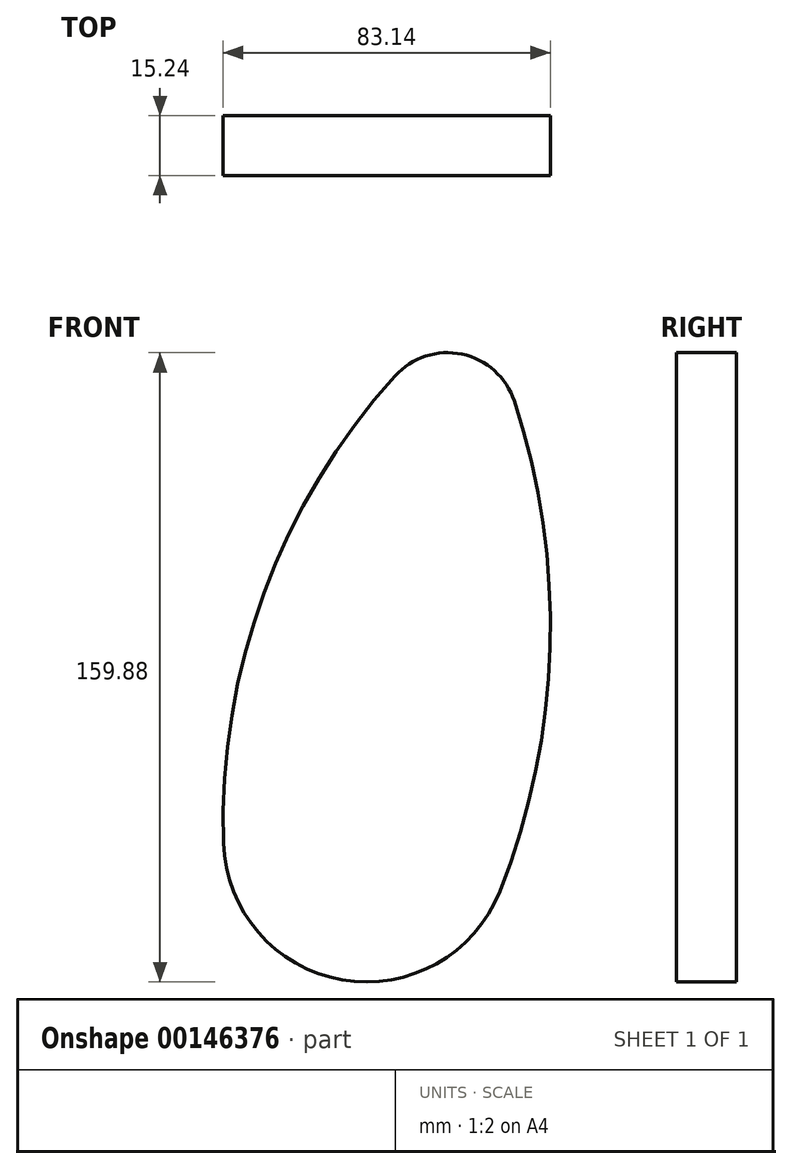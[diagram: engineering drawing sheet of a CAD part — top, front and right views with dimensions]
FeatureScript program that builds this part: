
annotation { "Feature Type Name" : "Feature", "Feature Type Description" : "" }
export const myFeature = defineFeature(function(context is Context, id is Id, definition is map)
    precondition{}
    {
        {
            var Q0;
            Q0=qCreatedBy(makeId("Front.planeOp"),FACE);
            var sketch = newSketch(context, id + "F0", { "sketchPlane" : qUnion([Q0])});
            skArc(sketch, "E0", {"start": v(31.42, 67.88) * mm, "mid": v(18.12, 79.8) * mm, "end": v(1.12, 74.29) * mm});
            skArc(sketch, "E1", {"start": v(1.12, 74.29) * mm, "mid": v(-32.17, 19.17) * mm, "end": v(-42.48, -44.4) * mm});
            skArc(sketch, "E2", {"start": v(-42.48, -44.4) * mm, "mid": v(-12.38, -79.14) * mm, "end": v(27.73, -56.69) * mm});
            skArc(sketch, "E3", {"start": v(27.73, -56.69) * mm, "mid": v(40.5, 5.27) * mm, "end": v(31.42, 67.88) * mm});
            skSolve(sketch);
        }
        {
            var Q0;
            Q0=makeQuery(id+"F0.imprint","IMPRINT",FACE,{"disambiguationData":[TD([[makeQuery(id+"F0.imprint","IMPRINT",EDGE,{"derivedFrom":sQuery(id+"F0.wireOp",EDGE,"E0")}),1.0]])]});
            extrude(context, id + "F1", {"entities" : qUnion([Q0]), "depth" : 15.24 * mm});
        }
    });
